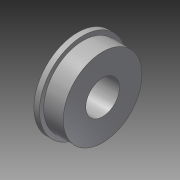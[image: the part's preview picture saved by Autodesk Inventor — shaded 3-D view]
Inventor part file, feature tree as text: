
AUTODESK INVENTOR PART (.ipt)
format: ipt  version: 2014 SP1 (Build 180222100, 222)  size: 99,840 bytes
history: native  units: in
note: dims shown in document units (in); Inventor stores cm internally (conversion verified against a paired STEP export)
features: revolve x1, other x1, imported_body x1
ambient origin geometry x8: Origin, YZ Plane, XZ Plane, XY Plane, X Axis, Y Axis, Z Axis, Center Point
bodies: Body1 (feature_tree)
feature tree (3):
  revolve  "Revolve1"  [1 undecoded]
  other  "217-2733.ipt1"
  imported_body  "Base1"
note: 1 required parameter value undecoded (feature->parameter linkage not recoverable at this tier; creation-order binding heuristic only, values carry confidence <= 0.55)
